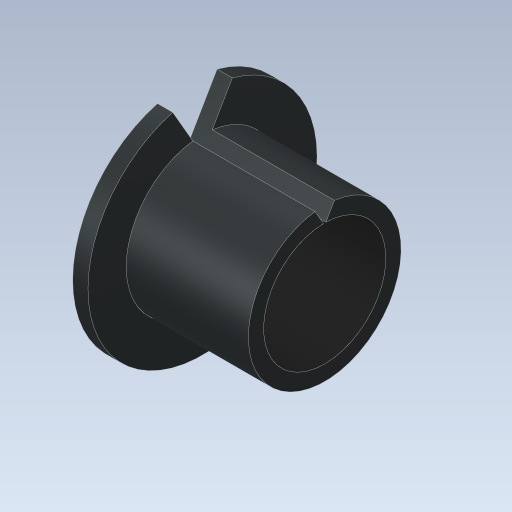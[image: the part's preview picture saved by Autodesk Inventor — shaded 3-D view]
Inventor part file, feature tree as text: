
AUTODESK INVENTOR PART (.ipt)
format: ipt  version: 2024 (Build 280153000, 153)  size: 144,384 bytes
history: native  units: mm
features: sketch x2, revolve x1, extrude x1
ambient origin geometry x8: Origin, YZ Plane, XZ Plane, XY Plane, X Axis, Y Axis, Z Axis, Center Point
bodies: Solid1 (feature_tree)
feature tree (4):
  revolve  "Revolution1"  [1 undecoded]
  extrude  "Extrusion1"  [1 undecoded]
  sketch  "Sketch_1"  dims[d0=360.0deg d1=9.0mm d2=0.0mm]
  sketch  "Sketch_3"
note: 2 required parameter values undecoded (feature->parameter linkage not recoverable at this tier; creation-order binding heuristic only, values carry confidence <= 0.55)